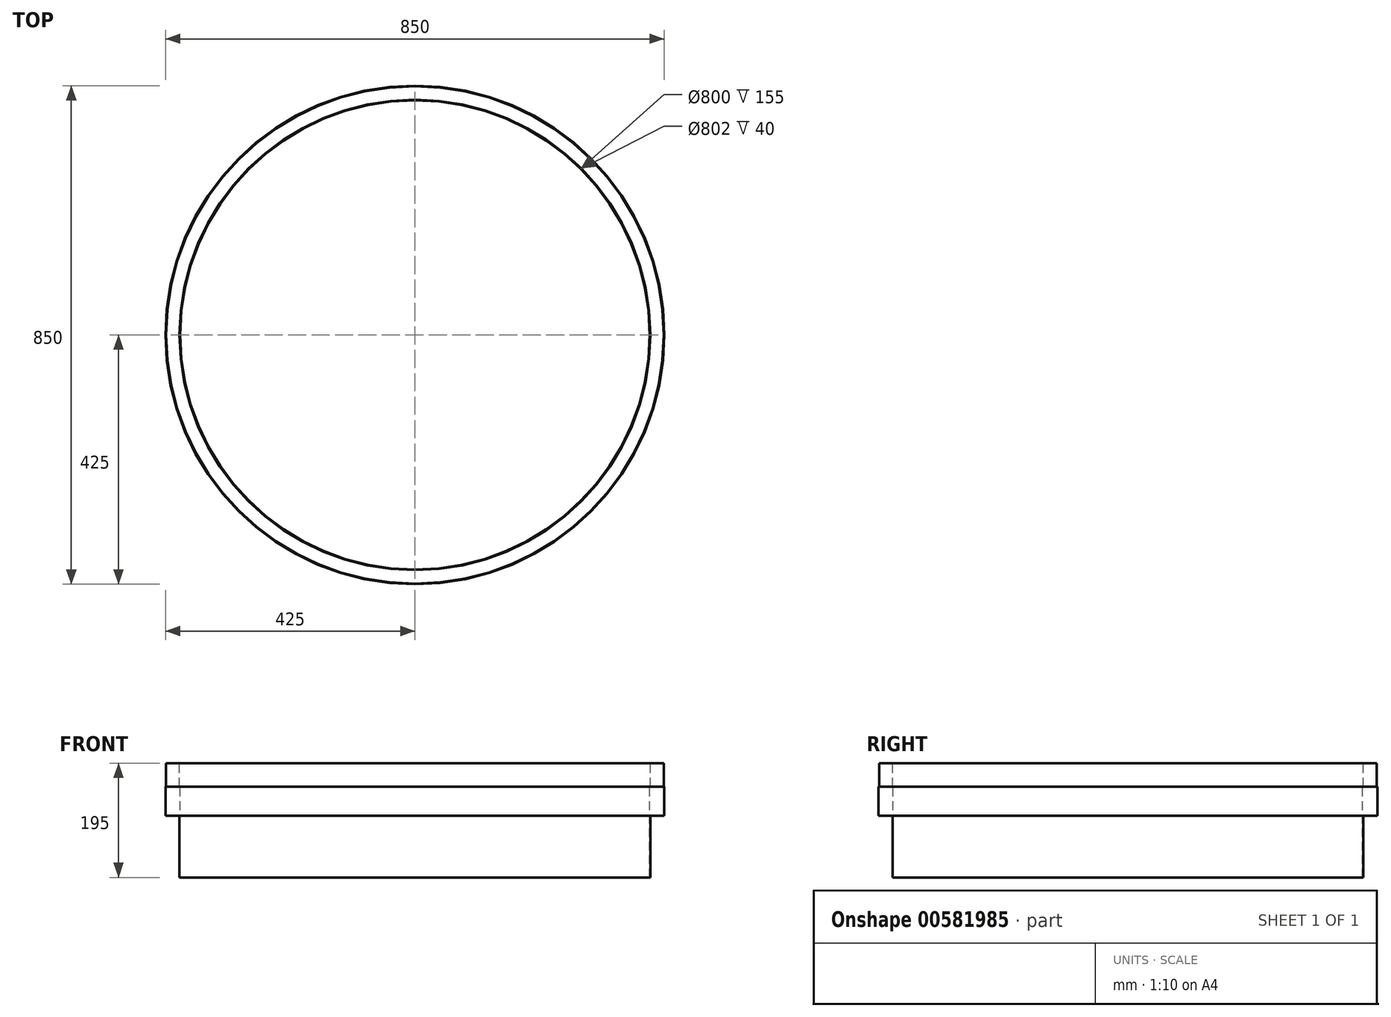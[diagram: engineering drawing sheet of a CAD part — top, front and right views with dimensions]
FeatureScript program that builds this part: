
annotation { "Feature Type Name" : "Feature", "Feature Type Description" : "" }
export const myFeature = defineFeature(function(context is Context, id is Id, definition is map)
    precondition{}
    {
        {
            var Q0;
            Q0=qCreatedBy(makeId("Front.planeOp"),FACE);
            var sketch = newSketch(context, id + "F0", { "sketchPlane" : qUnion([Q0])});
            skLineSegment(sketch, "E0", {"start": v(0, 710.75) * mm, "end": v(0, -704.58) * mm, "construction": true});
            skLineSegment(sketch, "E1", {"start": v(-400, 295.65) * mm, "end": v(-400, 410.65) * mm});
            skLineSegment(sketch, "E2", {"start": v(-400, 410.65) * mm, "end": v(-401, 410.65) * mm});
            skLineSegment(sketch, "E3", {"start": v(-424, 410.65) * mm, "end": v(-425, 410.65) * mm});
            skLineSegment(sketch, "E4", {"start": v(-425, 410.65) * mm, "end": v(-425, 360.65) * mm});
            skLineSegment(sketch, "E5", {"start": v(-425, 360.65) * mm, "end": v(-401, 360.65) * mm});
            skLineSegment(sketch, "E6", {"start": v(-401, 360.65) * mm, "end": v(-401, 295.65) * mm});
            skLineSegment(sketch, "E7", {"start": v(-424, 450.65) * mm, "end": v(-424, 410.65) * mm});
            skLineSegment(sketch, "E8", {"start": v(-424, 450.65) * mm, "end": v(-401, 450.65) * mm});
            skLineSegment(sketch, "E9", {"start": v(-401, 410.65) * mm, "end": v(-401, 450.65) * mm});
            skLineSegment(sketch, "E10", {"start": v(-400, 295.65) * mm, "end": v(-400, 255.65) * mm});
            skLineSegment(sketch, "E11", {"start": v(-401, 295.65) * mm, "end": v(-401, 255.65) * mm});
            skLineSegment(sketch, "E12", {"start": v(-401, 255.65) * mm, "end": v(-400, 255.65) * mm});
            skSolve(sketch);
        }
        {
            var Q0;
            Q0=qSketchRegion(id+"F0",true);
            var Q1;
            Q1=sQuery(id+"F0.wireOp",EDGE,"E0");
            revolve(context, id + "F1", {"entities" : qUnion([Q0]), "axis" : qUnion([Q1]), "revolveType" : RevolveType.FULL});
        }
    });
